# Revit family: ASH_Contour21_S0439_BIM_GB
name_source: partatom
category: Plumbing Fixtures
revit_build: Autodesk Revit 2015 (Build: 20140606_1530(x64)
units: mm (PartAtom-declared; Revit-internal decimal feet)

## types (1)
- S0439HY - Contour 21+ Back-to wall rimless WC bowl - hygenic+ glaze
    Accessories = www.idealspec.co.uk
    AreaUnits = millimeters
    Assembly Code = C1030200
    AssetType = Fixed
    BIMObjectName = ASH_ArmitageShanks_WCPans_Contour21Plus_S0439HY
    Brand = Armitage Shanks
    CWFU = 0
    ConnectionType = Plumbing
    Cost = 0 $
    Default Elevation = 410 mm
    Description = Contour 21+ back to wall rimless WC pan with raised horizontal outlet and anti-microbial glaze
    DurationUnit = year
    ExpectedLife = 30
    Features = back to wall rimless WC pan with raised horizontal outlet and anti-microbial glaze
    Finish = White
    HWFU = 0
    Help = www.idealspec.co.uk/contact-us.html
    IfcExportAs = IfcSanitaryTerminalType
    IfcExportType = TOILETPAN
    InstallationInstructions = www.idealspec.co.uk/resources.html
    LinearUnits = millimeters
    ManufacturerURL = www.idealspec.co.uk
    Model = S0439HY
    ModelNumber = S0439HY
    ModelReference = Contour 21+ back to wall rimless WC pan with raised horizontal outlet and anti-microbial glaze
    NBSDescription = WC pans
    NBSReference = 45-30-70/384
    Name = WCPans_Contour21Plus_S0439HY_ArmitageShanks
    NettWeight = 23.9 Kg
    NominalDepth = 520 mm  [stored 1.70604 ft]
    NominalHeight = 410 mm
    NominalLength = 520 mm  [stored 1.70604 ft]
    NominalWidth = 360 mm
    PanColor = White
    PanMaterial = Vitreous china
    PanMounting = BackToWall
    ProductInformation = www.idealspec.co.uk/assets/datasheet/S0439HY
    Shape = Sculptured
    Size = 410 x 520 x 360 mm
    Space = Internal
    SpareParts = www.fastpart-spares.co.uk
    SpilloverLevel = 410 mm
    ToiletPanType = WashDown
    ToiletType = Other
    URL = www.idealspec.co.uk
    Uniclass2015Code = Pr_40_20_93_94
    Uniclass2015Title = WC pans
    Uniclass2015Version = Products v1.1
    Version = 1
    VolumeUnits = Litres
    WFU = 0
    WarrantyDescription = Manufacturers Warranty
    WarrantyDurationParts = 99
    WarrantyDurationUnit = year

note: [stored X ft] marks values corroborated as IEEE doubles in the binary element streams (Revit-internal decimal feet)

## geometry (parser evidence)
native form markers: Blend x4, Sweep x2
no freeform markers — native parametric forms only
